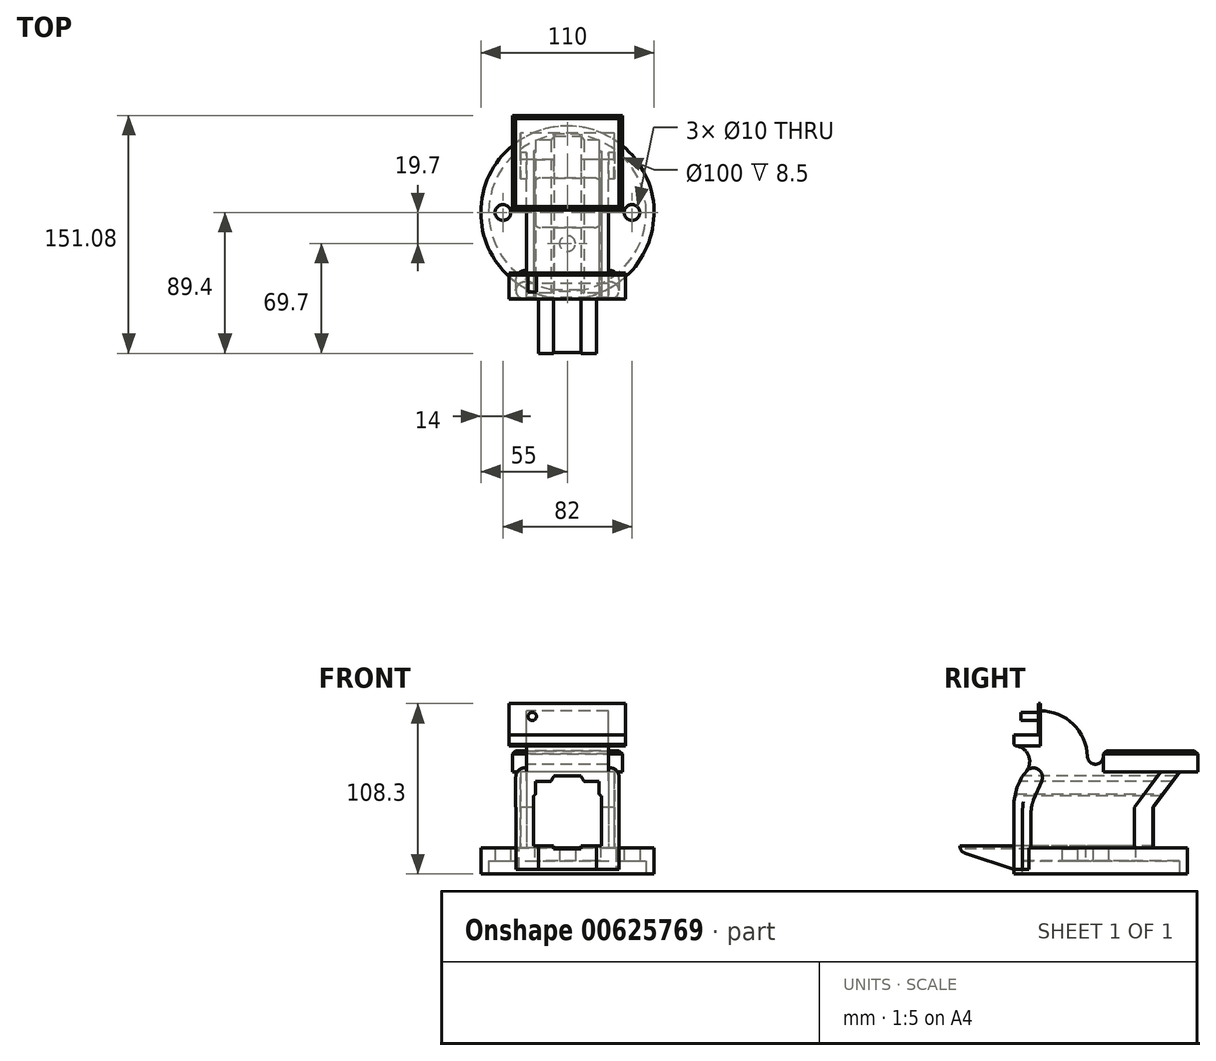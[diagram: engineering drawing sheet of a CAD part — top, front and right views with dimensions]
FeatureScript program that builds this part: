
annotation { "Feature Type Name" : "Feature", "Feature Type Description" : "" }
export const myFeature = defineFeature(function(context is Context, id is Id, definition is map)
    precondition{}
    {
        {
            var Q0;
            Q0=qCreatedBy(makeId("Front.planeOp"),FACE);
            var sketch = newSketch(context, id + "F0", { "sketchPlane" : qUnion([Q0])});
            skLineSegment(sketch, "E0", {"start": v(0, 0) * mm, "end": v(0, 5.39) * mm, "construction": true});
            skLineSegment(sketch, "E1", {"start": v(0, 16.6) * mm, "end": v(55, 16.6) * mm});
            skLineSegment(sketch, "E2", {"start": v(55, 16.6) * mm, "end": v(55, 0) * mm});
            skLineSegment(sketch, "E3", {"start": v(55, 0) * mm, "end": v(50, 0) * mm});
            skLineSegment(sketch, "E4", {"start": v(50, 0) * mm, "end": v(50, 8.5) * mm});
            skLineSegment(sketch, "E5", {"start": v(50, 8.5) * mm, "end": v(0, 8.5) * mm});
            skLineSegment(sketch, "E6", {"start": v(0, 8.5) * mm, "end": v(0, 16.6) * mm});
            skSolve(sketch);
        }
        {
            var Q0;
            Q0=makeQuery(id+"F0.imprint","IMPRINT",FACE,{"disambiguationData":[TD([[makeQuery(id+"F0.imprint","IMPRINT",EDGE,{"derivedFrom":sQuery(id+"F0.wireOp",EDGE,"E1")}),-1.0]])]});
            var Q1;
            Q1=sQuery(id+"F0.wireOp",EDGE,"E0");
            revolve(context, id + "F1", {"entities" : qUnion([Q0]), "axis" : qUnion([Q1]), "revolveType" : RevolveType.FULL});
        }
        {
            var Q0;
            Q0=qCreatedBy(makeId("Front.planeOp"),FACE);
            cPlane(context, id + "F2", {"entities" : qUnion([Q0]), "cplaneType" : CPlaneType.OFFSET, "offset" : 55 * mm, "width" : 150 * mm, "height" : 150 * mm});
        }
        {
            var Q0;
            Q0=qCreatedBy(makeId("Right.planeOp"),FACE);
            var sketch = newSketch(context, id + "F3", { "sketchPlane" : qUnion([Q0])});
            skLineSegment(sketch, "E7", {"start": v(-55, 16.6) * mm, "end": v(33.65, 16.6) * mm});
            skLineSegment(sketch, "E8", {"start": v(33.65, 16.6) * mm, "end": v(33.65, 42.45) * mm});
            skLineSegment(sketch, "E9", {"start": v(61.68, 65.05) * mm, "end": v(61.68, 78.25) * mm});
            skLineSegment(sketch, "E10", {"start": v(-38.3, 81.53) * mm, "end": v(-38.3, 108.3) * mm});
            skLineSegment(sketch, "E11", {"start": v(-38.3, 108.3) * mm, "end": v(-50.5, 108.3) * mm});
            skLineSegment(sketch, "E12", {"start": v(-50.5, 108.3) * mm, "end": v(-50.5, 88.53) * mm});
            skLineSegment(sketch, "E13", {"start": v(-55, 88.53) * mm, "end": v(-55, 81.53) * mm});
            skLineSegment(sketch, "E14", {"start": v(-55, 81.53) * mm, "end": v(-38.3, 81.53) * mm});
            skLineSegment(sketch, "E15", {"start": v(-55, 3) * mm, "end": v(-55, 16.6) * mm});
            skLineSegment(sketch, "E16", {"start": v(-55, 3) * mm, "end": v(-85.97, 13.25) * mm});
            skLineSegment(sketch, "E17", {"start": v(-89.4, 18) * mm, "end": v(-55, 18) * mm});
            skLineSegment(sketch, "E18", {"start": v(-55, 18) * mm, "end": v(-55, 43.25) * mm});
            skArc(sketch, "E19.filletArc", {"start": v(-47.22, 65.25) * mm, "mid": v(-53, 54.92) * mm, "end": v(-55, 43.25) * mm});
            skArc(sketch, "E20", {"start": v(-47.22, 65.25) * mm, "mid": v(-45.98, 75.84) * mm, "end": v(-55, 81.53) * mm});
            skLineSegment(sketch, "E21", {"start": v(1.68, 78.25) * mm, "end": v(61.68, 78.25) * mm});
            skPoint(sketch, "E22.visualSharp", {"position": v(-99.35, 17.68) * mm});
            skArc(sketch, "E22.filletArc", {"start": v(-89.4, 18) * mm, "mid": v(-88.45, 15.07) * mm, "end": v(-85.97, 13.25) * mm});
            skLineSegment(sketch, "E23", {"start": v(61.68, 65.05) * mm, "end": v(54.21, 65.05) * mm});
            skPoint(sketch, "E24.orphan", {"position": v(-20, 78.25) * mm});
            skLineSegment(sketch, "E25", {"start": v(61.68, 65.05) * mm, "end": v(50.38, 65.05) * mm});
            skLineSegment(sketch, "E26", {"start": v(50.38, 65.05) * mm, "end": v(33.65, 42.45) * mm});
            skPoint(sketch, "E27", {"position": v(-45, 71.53) * mm});
            skArc(sketch, "E28", {"start": v(-8.31, 74.6) * mm, "mid": v(-17.4, 95.23) * mm, "end": v(-38.3, 103.7) * mm});
            skPoint(sketch, "E29", {"position": v(-38.3, 103.7) * mm});
            skPoint(sketch, "E30", {"position": v(-8.3, 73.7) * mm});
            skLineSegment(sketch, "E31", {"start": v(-58.58, 103.7) * mm, "end": v(-30.24, 103.7) * mm, "construction": true});
            skArc(sketch, "E32", {"start": v(-8.31, 74.6) * mm, "mid": v(-3.24, 69.75) * mm, "end": v(1.68, 74.75) * mm});
            skPoint(sketch, "E33", {"position": v(1.68, 74.75) * mm});
            skLineSegment(sketch, "E34", {"start": v(1.68, 78.25) * mm, "end": v(1.68, 74.75) * mm});
            skLineSegment(sketch, "E35", {"start": v(1.68, 74.75) * mm, "end": v(1.68, 65.05) * mm});
            skLineSegment(sketch, "E36", {"start": v(1.68, 65.05) * mm, "end": v(50.38, 65.05) * mm});
            skLineSegment(sketch, "E37", {"start": v(-55, 88.53) * mm, "end": v(-50.5, 88.53) * mm});
            skCircle(sketch, "E38", {"center": v(-42.7, 61.59) * mm, "radius": 5.83 * mm});
            skLineSegment(sketch, "E39", {"start": v(-55, 71.53) * mm, "end": v(-42.7, 61.59) * mm, "construction": true});
            skLineSegment(sketch, "E40", {"start": v(-37.32, 59.32) * mm, "end": v(-42.53, 46.98) * mm});
            skLineSegment(sketch, "E41", {"start": v(-44.1, 39.2) * mm, "end": v(-44.1, 16.6) * mm});
            skPoint(sketch, "E42.visualSharp", {"position": v(-44.1, 43.25) * mm});
            skArc(sketch, "E42.filletArc", {"start": v(-42.53, 46.98) * mm, "mid": v(-43.7, 43.17) * mm, "end": v(-44.1, 39.2) * mm});
            skLineSegment(sketch, "E43", {"start": v(-55, 18) * mm, "end": v(-55, 3) * mm});
            skLineSegment(sketch, "E44", {"start": v(-55, 16.6) * mm, "end": v(-55, 3) * mm});
            skLineSegment(sketch, "E45", {"start": v(-55, 3) * mm, "end": v(-44.1, 3) * mm});
            skLineSegment(sketch, "E46", {"start": v(-44.1, 3) * mm, "end": v(-44.1, 16.6) * mm});
            skLineSegment(sketch, "E47", {"start": v(38.08, 65.05) * mm, "end": v(21.35, 42.45) * mm});
            skLineSegment(sketch, "E48", {"start": v(21.35, 42.45) * mm, "end": v(21.35, 16.6) * mm});
            skLineSegment(sketch, "E49", {"start": v(61.68, 65.05) * mm, "end": v(61.68, -19.1) * mm, "construction": true});
            skLineSegment(sketch, "E50", {"start": v(55, 37.37) * mm, "end": v(55, 23.13) * mm, "construction": true});
            skArc(sketch, "E51", {"start": v(-47.22, 65.25) * mm, "mid": v(-29.57, 76.92) * mm, "end": v(-8.41, 76.28) * mm, "construction": true});
            skSolve(sketch);
        }
        {
            var Q0;
            {var subQ3=sQuery(id+"F3.wireOp",EDGE,"E14");Q0=makeQuery(id+"F3.imprint","IMPRINT",FACE,{"disambiguationData":[TD([[makeQuery(id+"F3.imprint","IMPRINT",EDGE,{"derivedFrom":subQ3}),-1.0]])]});}
            extrude(context, id + "F4", {"entities" : qUnion([Q0]), "operationType" : NewBodyOperationType.ADD, "depth" : 52 * mm, "offsetDistance" : 25 * mm, "symmetric" : true});
        }
        {
            var Q0;
            {var subQ1=sQuery(id+"F3.wireOp",EDGE,"E9");Q0=makeQuery(id+"F3.imprint","IMPRINT",FACE,{"disambiguationData":[TD([[makeQuery(id+"F3.imprint","IMPRINT",EDGE,{"derivedFrom":subQ1}),1.0]])]});}
            extrude(context, id + "F5", {"entities" : qUnion([Q0]), "operationType" : NewBodyOperationType.ADD, "depth" : 69.7 * mm, "offsetDistance" : 25 * mm, "symmetric" : true});
        }
        {
            var Q0;
            {var subQ0=sQuery(id+"F3.wireOp",EDGE,"E11");Q0=makeQuery(id+"F3.imprint","IMPRINT",FACE,{"disambiguationData":[TD([[makeQuery(id+"F3.imprint","IMPRINT",EDGE,{"derivedFrom":subQ0}),1.0]])]});}
            extrude(context, id + "F6", {"entities" : qUnion([Q0]), "operationType" : NewBodyOperationType.ADD, "depth" : 74 * mm, "offsetDistance" : 25 * mm, "symmetric" : true});
        }
        {
            var Q0;
            {var subQ1=sQuery(id+"F3.wireOp",EDGE,"E15");Q0=makeQuery(id+"F3.imprint","IMPRINT",FACE,{"disambiguationData":[TD([[makeQuery(id+"F3.imprint","IMPRINT",EDGE,{"derivedFrom":subQ1}),-1.0]])]});}
            var Q1;
            {var subQ0=sQuery(id+"F3.wireOp",EDGE,"E38");var subQ2=makeQuery(id+"F3.imprint","INTERSECT",VERTEX,{"derivedFrom":[subQ0,sQuery(id+"F3.wireOp",EDGE,"E40")]});Q1=makeQuery(id+"F3.imprint","IMPRINT",FACE,{"disambiguationData":[TD([[makeQuery(id+"F3.imprint","IMPRINT",EDGE,{"disambiguationData":[TD([[subQ2,1.0]])],"derivedFrom":subQ0}),1.0]])]});}
            var Q2;
            {var subQ0=sQuery(id+"F3.wireOp",EDGE,"E44");Q2=makeQuery(id+"F3.imprint","IMPRINT",FACE,{"disambiguationData":[TD([[makeQuery(id+"F3.imprint","IMPRINT",EDGE,{"derivedFrom":subQ0}),1.0]])]});}
            var Q3;
            Q3=makeQuery(id+"F3.imprint","IMPRINT",FACE,{"disambiguationData":[TD([[makeQuery(id+"F3.imprint","IMPRINT",EDGE,{"derivedFrom":sQuery(id+"F3.wireOp",EDGE,"E18")}),-1.0]])]});
            extrude(context, id + "F7", {"entities" : qUnion([Q0, Q1, Q2, Q3]), "operationType" : NewBodyOperationType.ADD, "depth" : 65.65 * mm, "offsetDistance" : 25 * mm, "symmetric" : true});
        }
        {
            var Q0;
            Q0=makeQuery(id+"F3.imprint","IMPRINT",FACE,{"disambiguationData":[TD([[makeQuery(id+"F3.imprint","IMPRINT",EDGE,{"derivedFrom":sQuery(id+"F3.wireOp",EDGE,"E16")}),-1.0]])]});
            extrude(context, id + "F8", {"entities" : qUnion([Q0]), "operationType" : NewBodyOperationType.ADD, "depth" : 37 * mm, "offsetDistance" : 25 * mm, "symmetric" : true});
        }
        {
            var Q0;
            Q0=makeQuery(id+"F5.opExtrude","SWEPT_EDGE",EDGE,{"disambiguationData":[OSD([sQuery(id+"F3.wireOp",EDGE,"E21"),sQuery(id+"F3.wireOp",EDGE,"E34")])]});
            var Q1;
            Q1=makeQuery(id+"F5.opExtrude","CAP_EDGE",EDGE,{"disambiguationData":[OSD([sQuery(id+"F3.wireOp",EDGE,"E21")])],"isStart":false});
            var Q2;
            Q2=makeQuery(id+"F5.opExtrude","SWEPT_EDGE",EDGE,{"disambiguationData":[OSD([sQuery(id+"F3.wireOp",EDGE,"E9"),sQuery(id+"F3.wireOp",EDGE,"E21")])]});
            var Q3;
            Q3=makeQuery(id+"F5.opExtrude","CAP_EDGE",EDGE,{"disambiguationData":[OSD([sQuery(id+"F3.wireOp",EDGE,"E21")])],"isStart":true});
            chamfer(context, id + "F9", {"entities" : qUnion([Q0, Q1, Q2, Q3]), "width" : 2 * mm, "tangentPropagation" : true});
        }
        {
            var Q0;
            Q0=makeQuery(id+"F7.opExtrude","CAP_EDGE",EDGE,{"disambiguationData":[OSD([sQuery(id+"F3.wireOp",EDGE,"E38")])],"isStart":false});
            var Q1;
            Q1=makeQuery(id+"F7.opExtrude","CAP_EDGE",EDGE,{"disambiguationData":[OSD([sQuery(id+"F3.wireOp",EDGE,"E19.filletArc")])],"isStart":false});
            var Q2;
            Q2=makeQuery(id+"F7.opExtrude","CAP_EDGE",EDGE,{"disambiguationData":[OSD([sQuery(id+"F3.wireOp",EDGE,"E18"),sQuery(id+"F3.wireOp",EDGE,"E43"),sQuery(id+"F3.wireOp",EDGE,"E44")])],"isStart":false});
            var Q3;
            Q3=makeQuery(id+"F7.opExtrude","CAP_EDGE",EDGE,{"disambiguationData":[OSD([sQuery(id+"F3.wireOp",EDGE,"E40")])],"isStart":false});
            var Q4;
            Q4=makeQuery(id+"F7.opExtrude","CAP_EDGE",EDGE,{"disambiguationData":[OSD([sQuery(id+"F3.wireOp",EDGE,"E42.filletArc")])],"isStart":false});
            var Q5;
            Q5=makeQuery(id+"F7.opExtrude","CAP_EDGE",EDGE,{"disambiguationData":[OSD([sQuery(id+"F3.wireOp",EDGE,"E41"),sQuery(id+"F3.wireOp",EDGE,"E46")])],"isStart":false});
            var Q6;
            Q6=makeQuery(id+"F7.opExtrude","CAP_EDGE",EDGE,{"disambiguationData":[OSD([sQuery(id+"F3.wireOp",EDGE,"E19.filletArc")])],"isStart":true});
            fillet(context, id + "F10", {"entities" : qUnion([Q0, Q1, Q2, Q3, Q4, Q5, Q6]), "radius" : 5.83 * mm, "tangentPropagation" : true, "allowEdgeOverflow" : false});
        }
        {
            var Q0;
            {var subQ3=sQuery(id+"F3.wireOp",EDGE,"E8");Q0=makeQuery(id+"F3.imprint","IMPRINT",FACE,{"disambiguationData":[TD([[makeQuery(id+"F3.imprint","IMPRINT",EDGE,{"derivedFrom":subQ3}),1.0]])]});}
            extrude(context, id + "F11", {"entities" : qUnion([Q0]), "operationType" : NewBodyOperationType.ADD, "depth" : 59.9 * mm, "offsetDistance" : 25 * mm, "symmetric" : true});
        }
        {
            var Q0;
            Q0=makeQuery(id+"F11.opExtrude","CAP_EDGE",EDGE,{"disambiguationData":[OSD([sQuery(id+"F3.wireOp",EDGE,"E47")])],"isStart":false});
            var Q1;
            Q1=makeQuery(id+"F11.opExtrude","CAP_EDGE",EDGE,{"disambiguationData":[OSD([sQuery(id+"F3.wireOp",EDGE,"E48")])],"isStart":false});
            var Q2;
            Q2=makeQuery(id+"F11.opExtrude","CAP_EDGE",EDGE,{"disambiguationData":[OSD([sQuery(id+"F3.wireOp",EDGE,"E8")])],"isStart":false});
            var Q3;
            Q3=makeQuery(id+"F11.opExtrude","CAP_EDGE",EDGE,{"disambiguationData":[OSD([sQuery(id+"F3.wireOp",EDGE,"E26")])],"isStart":false});
            var Q4;
            Q4=makeQuery(id+"F11.opExtrude","CAP_EDGE",EDGE,{"disambiguationData":[OSD([sQuery(id+"F3.wireOp",EDGE,"E26")])],"isStart":true});
            var Q5;
            Q5=makeQuery(id+"F11.opExtrude","CAP_EDGE",EDGE,{"disambiguationData":[OSD([sQuery(id+"F3.wireOp",EDGE,"E8")])],"isStart":true});
            var Q6;
            Q6=makeQuery(id+"F11.opExtrude","CAP_EDGE",EDGE,{"disambiguationData":[OSD([sQuery(id+"F3.wireOp",EDGE,"E48")])],"isStart":true});
            var Q7;
            Q7=makeQuery(id+"F11.opExtrude","CAP_EDGE",EDGE,{"disambiguationData":[OSD([sQuery(id+"F3.wireOp",EDGE,"E47")])],"isStart":true});
            chamfer(context, id + "F12", {"entities" : qUnion([Q0, Q1, Q2, Q3, Q4, Q5, Q6, Q7]), "width" : .3 * mm, "tangentPropagation" : true});
        }
        {
            var Q0;
            Q0=makeQuery(id+"F7.opExtrude","SWEPT_FACE",FACE,{"disambiguationData":[OSD([sQuery(id+"F3.wireOp",EDGE,"E18"),sQuery(id+"F3.wireOp",EDGE,"E43"),sQuery(id+"F3.wireOp",EDGE,"E44")])]});
            var sketch = newSketch(context, id + "F13", { "sketchPlane" : qUnion([Q0])});
            skLineSegment(sketch, "E52.bottom", {"start": v(-21.6, 18) * mm, "end": v(21.6, 18) * mm});
            skLineSegment(sketch, "E52.top", {"start": v(-20.15, 59) * mm, "end": v(20.15, 59) * mm});
            skLineSegment(sketch, "E52.left", {"start": v(-21.6, 18) * mm, "end": v(-21.6, 49.8) * mm});
            skLineSegment(sketch, "E52.right", {"start": v(21.6, 18) * mm, "end": v(21.6, 49.8) * mm});
            skPoint(sketch, "E53", {"position": v(0, 18) * mm});
            skLineSegment(sketch, "E54", {"start": v(-21.6, 49.8) * mm, "end": v(-20.15, 49.8) * mm});
            skLineSegment(sketch, "E55", {"start": v(-20.15, 49.8) * mm, "end": v(-20.15, 59) * mm});
            skLineSegment(sketch, "E56", {"start": v(0, 0) * mm, "end": v(0, 68.14) * mm, "construction": true});
            skPoint(sketch, "E56.endSnap0", {"position": v(0, 59) * mm});
            skLineSegment(sketch, "E57.MirrorCS", {"start": v(20.15, 49.8) * mm, "end": v(20.15, 59) * mm});
            skLineSegment(sketch, "E58.MirrorCS", {"start": v(21.6, 49.8) * mm, "end": v(20.15, 49.8) * mm});
            skLineSegment(sketch, "E59", {"start": v(-10.45, 59) * mm, "end": v(-8.5, 62.38) * mm});
            skLineSegment(sketch, "E60", {"start": v(-8.5, 62.38) * mm, "end": v(0, 62.38) * mm});
            skLineSegment(sketch, "E61.MirrorCS", {"start": v(8.5, 62.38) * mm, "end": v(0, 62.38) * mm});
            skLineSegment(sketch, "E62.MirrorCS", {"start": v(10.45, 59) * mm, "end": v(8.5, 62.38) * mm});
            skPoint(sketch, "E63.orphan", {"position": v(-21.6, 59) * mm});
            skPoint(sketch, "E64.orphan", {"position": v(21.6, 59) * mm});
            skLineSegment(sketch, "E65", {"start": v(-8.72, 18) * mm, "end": v(-8.72, 16) * mm});
            skLineSegment(sketch, "E66", {"start": v(-8.72, 16) * mm, "end": v(0, 16) * mm});
            skLineSegment(sketch, "E67.MirrorCS", {"start": v(8.72, 16) * mm, "end": v(0, 16) * mm});
            skLineSegment(sketch, "E68.MirrorCS", {"start": v(8.73, 18) * mm, "end": v(8.73, 16) * mm});
            skSolve(sketch);
        }
        {
            var Q0;
            {var subQ0=sQuery(id+"F13.wireOp",EDGE,"E59");Q0=makeQuery(id+"F13.imprint","IMPRINT",FACE,{"disambiguationData":[TD([[makeQuery(id+"F13.imprint","IMPRINT",EDGE,{"derivedFrom":subQ0}),-1.0]])]});}
            var Q1;
            {var subQ0=sQuery(id+"F13.wireOp",EDGE,"E54");Q1=makeQuery(id+"F13.imprint","IMPRINT",FACE,{"disambiguationData":[TD([[makeQuery(id+"F13.imprint","IMPRINT",EDGE,{"derivedFrom":subQ0}),-1.0]])]});}
            var Q2;
            {var subQ0=sQuery(id+"F13.wireOp",EDGE,"E52.bottom");var subQ6=makeQuery(id+"F13.imprint","INTERSECT",VERTEX,{"derivedFrom":[subQ0,sQuery(id+"F13.wireOp",EDGE,"E65")]});Q2=makeQuery(id+"F13.imprint","IMPRINT",FACE,{"disambiguationData":[TD([[makeQuery(id+"F13.imprint","IMPRINT",EDGE,{"disambiguationData":[TD([[subQ6,1.0]])],"derivedFrom":subQ0}),-1.0]])]});}
            var Q3;
            {var subQ0=sQuery(id+"F13.wireOp",EDGE,"E65");Q3=makeQuery(id+"F13.imprint","IMPRINT",FACE,{"disambiguationData":[TD([[makeQuery(id+"F13.imprint","IMPRINT",EDGE,{"derivedFrom":subQ0}),1.0]])]});}
            extrude(context, id + "F14", {"entities" : qUnion([Q0, Q1, Q2, Q3]), "operationType" : NewBodyOperationType.REMOVE, "endBound" : BoundingType.THROUGH_ALL, "oppositeDirection" : true, "depth" : 25 * mm, "offsetDistance" : 25 * mm, "hasSecondDirection" : true, "secondDirectionBound" : BoundingType.THROUGH_ALL, "secondDirectionOppositeDirection" : false, "secondDirectionDepth" : 25 * mm});
        }
        {
            var Q0;
            {var subQ0=sQuery(id+"F3.wireOp",EDGE,"E20");var subQ1=sQuery(id+"F3.wireOp",EDGE,"E14");var subQ2=sQuery(id+"F3.wireOp",EDGE,"E13");Q0=makeQuery(id+"F6.boolean.opBoolean","MERGE",EDGE,{"derivedFrom":[makeQuery(id+"F4.opExtrude","SWEPT_EDGE",EDGE,{"disambiguationData":[OSD([subQ2,subQ1,subQ0])]}),makeQuery(id+"F6.opExtrude","SWEPT_EDGE",EDGE,{"disambiguationData":[OSD([subQ2,subQ1,subQ0])]})]});}
            var Q1;
            Q1=makeQuery(id+"F14.boolean.opBoolean","COPY",EDGE,{"derivedFrom":makeQuery(id+"F14.opExtrude","SWEPT_EDGE",EDGE,{"disambiguationData":[OSD([sQuery(id+"F13.wireOp",EDGE,"E54"),sQuery(id+"F13.wireOp",EDGE,"E55")])]})});
            var Q2;
            Q2=makeQuery(id+"F14.boolean.opBoolean","COPY",EDGE,{"derivedFrom":makeQuery(id+"F14.opExtrude","SWEPT_EDGE",EDGE,{"disambiguationData":[OSD([sQuery(id+"F13.wireOp",EDGE,"E57.MirrorCS"),sQuery(id+"F13.wireOp",EDGE,"E58.MirrorCS")])]})});
            chamfer(context, id + "F15", {"entities" : qUnion([Q0, Q1, Q2]), "width" : 1 * mm, "tangentPropagation" : true});
        }
        {
            var Q0;
            Q0=makeQuery(id+"F6.opExtrude","SWEPT_FACE",FACE,{"disambiguationData":[OSD([sQuery(id+"F3.wireOp",EDGE,"E12")])]});
            var sketch = newSketch(context, id + "F16", { "sketchPlane" : qUnion([Q0])});
            skLineSegment(sketch, "E69", {"start": v(0, 0) * mm, "end": v(0, 123.92) * mm, "construction": true});
            skCircle(sketch, "E70", {"center": v(22.35, 100.15) * mm, "radius": 2.65 * mm});
            skCircle(sketch, "E71.MirrorC", {"center": v(-22.35, 100.15) * mm, "radius": 2.65 * mm});
            skSolve(sketch);
        }
        {
            var Q0;
            Q0=makeQuery(id+"F16.imprint","IMPRINT",FACE,{"disambiguationData":[TD([[makeQuery(id+"F16.imprint","IMPRINT",EDGE,{"derivedFrom":sQuery(id+"F16.wireOp",EDGE,"E71.MirrorC")}),-1.0]])]});
            var Q1;
            Q1=makeQuery(id+"F16.imprint","IMPRINT",FACE,{"disambiguationData":[TD([[makeQuery(id+"F16.imprint","IMPRINT",EDGE,{"derivedFrom":sQuery(id+"F16.wireOp",EDGE,"E70")}),1.0]])]});
            extrude(context, id + "F17", {"entities" : qUnion([Q0, Q1]), "operationType" : NewBodyOperationType.REMOVE, "oppositeDirection" : true, "depth" : 10.95 * mm, "offsetDistance" : 25 * mm});
        }
        {
            var Q0;
            Q0=makeQuery(id+"F7.boolean.opBoolean","SPLIT",FACE,{"disambiguationData":[TD([makeQuery(id+"F1.opRevolve","SWEPT_FACE",FACE,{"disambiguationData":[OSD([sQuery(id+"F0.wireOp",EDGE,"E4")])]})])],"derivedFrom":makeQuery(id+"F7.opExtrude","SWEPT_FACE",FACE,{"disambiguationData":[OSD([sQuery(id+"F3.wireOp",EDGE,"E45")])]})});
            var Q1;
            Q1=makeQuery(id+"F1.opRevolve","SWEPT_FACE",FACE,{"disambiguationData":[OSD([sQuery(id+"F0.wireOp",EDGE,"E5")])]});
            extrude(context, id + "F18", {"entities" : qUnion([Q0]), "operationType" : NewBodyOperationType.REMOVE, "endBound" : BoundingType.UP_TO_SURFACE, "oppositeDirection" : true, "depth" : 25 * mm, "endBoundEntityFace" : qUnion([Q1]), "offsetDistance" : 25 * mm});
        }
        {
            var Q0;
            {var subQ0=sQuery(id+"F0.wireOp",EDGE,"E5");Q0=makeQuery(id+"F18.boolean.opBoolean","MERGE",FACE,{"derivedFrom":[makeQuery(id+"F1.opRevolve","SWEPT_FACE",FACE,{"disambiguationData":[OSD([subQ0])]}),makeQuery(id+"F18.opExtrude","CAP_FACE",FACE,{"disambiguationData":[OSD([subQ0])],"isStart":false})]});}
            var sketch = newSketch(context, id + "F19", { "sketchPlane" : qUnion([Q0])});
            skLineSegment(sketch, "E72.bottom", {"start": v(17, -22) * mm, "end": v(-17, -22) * mm});
            skLineSegment(sketch, "E72.top", {"start": v(17, 9.7) * mm, "end": v(-17, 9.7) * mm});
            skLineSegment(sketch, "E72.left", {"start": v(21, -18) * mm, "end": v(21, 5.7) * mm});
            skLineSegment(sketch, "E72.right", {"start": v(-21, -18) * mm, "end": v(-21, 5.7) * mm});
            skPoint(sketch, "E72.middle", {"position": v(0, -6.15) * mm});
            skPoint(sketch, "E73.visualSharp", {"position": v(-21, 9.7) * mm});
            skArc(sketch, "E73.filletArc", {"start": v(-17, 9.7) * mm, "mid": v(-19.83, 8.53) * mm, "end": v(-21, 5.7) * mm});
            skPoint(sketch, "E74.visualSharp", {"position": v(-21, -22) * mm});
            skArc(sketch, "E74.filletArc", {"start": v(-21, -18) * mm, "mid": v(-19.83, -20.83) * mm, "end": v(-17, -22) * mm});
            skPoint(sketch, "E75.visualSharp", {"position": v(21, -22) * mm});
            skArc(sketch, "E75.filletArc", {"start": v(17, -22) * mm, "mid": v(19.83, -20.83) * mm, "end": v(21, -18) * mm});
            skPoint(sketch, "E76.visualSharp", {"position": v(21, 9.7) * mm});
            skArc(sketch, "E76.filletArc", {"start": v(21, 5.7) * mm, "mid": v(19.83, 8.53) * mm, "end": v(17, 9.7) * mm});
            skCircle(sketch, "E77", {"center": v(0, 19.7) * mm, "radius": 5 * mm});
            skCircle(sketch, "E78", {"center": v(41, 0) * mm, "radius": 5 * mm});
            skCircle(sketch, "E79", {"center": v(-41, 0) * mm, "radius": 5 * mm});
            skSolve(sketch);
        }
        {
            var Q0;
            Q0=makeQuery(id+"F19.imprint","IMPRINT",FACE,{"disambiguationData":[TD([[makeQuery(id+"F19.imprint","IMPRINT",EDGE,{"derivedFrom":sQuery(id+"F19.wireOp",EDGE,"E72.bottom")}),-1.0]])]});
            var Q1;
            Q1=makeQuery(id+"F19.imprint","IMPRINT",FACE,{"disambiguationData":[TD([[makeQuery(id+"F19.imprint","IMPRINT",EDGE,{"derivedFrom":sQuery(id+"F19.wireOp",EDGE,"E77")}),1.0]])]});
            var Q2;
            Q2=makeQuery(id+"F19.imprint","IMPRINT",FACE,{"disambiguationData":[TD([[makeQuery(id+"F19.imprint","IMPRINT",EDGE,{"derivedFrom":sQuery(id+"F19.wireOp",EDGE,"E78")}),1.0]])]});
            var Q3;
            Q3=makeQuery(id+"F19.imprint","IMPRINT",FACE,{"disambiguationData":[TD([[makeQuery(id+"F19.imprint","IMPRINT",EDGE,{"derivedFrom":sQuery(id+"F19.wireOp",EDGE,"E79")}),1.0]])]});
            extrude(context, id + "F20", {"entities" : qUnion([Q0, Q1, Q2, Q3]), "operationType" : NewBodyOperationType.REMOVE, "endBound" : BoundingType.UP_TO_NEXT, "oppositeDirection" : true, "depth" : 25 * mm, "offsetDistance" : 25 * mm});
        }
        {
            var Q0;
            Q0=makeQuery(id+"F20.boolean.opBoolean","SPLIT",FACE,{"disambiguationData":[TD([makeQuery(id+"F1.opRevolve","SWEPT_FACE",FACE,{"disambiguationData":[OSD([sQuery(id+"F0.wireOp",EDGE,"E2")])]})])],"derivedFrom":makeQuery(id+"F14.boolean.opBoolean","COPY",FACE,{"derivedFrom":makeQuery(id+"F14.opExtrude","SWEPT_FACE",FACE,{"disambiguationData":[OSD([sQuery(id+"F13.wireOp",EDGE,"E66"),sQuery(id+"F13.wireOp",EDGE,"E67.MirrorCS")])]})})});
            extrude(context, id + "F21", {"entities" : qUnion([Q0]), "operationType" : NewBodyOperationType.ADD, "depth" : 0.6 * mm, "offsetDistance" : 25 * mm});
        }
    });
